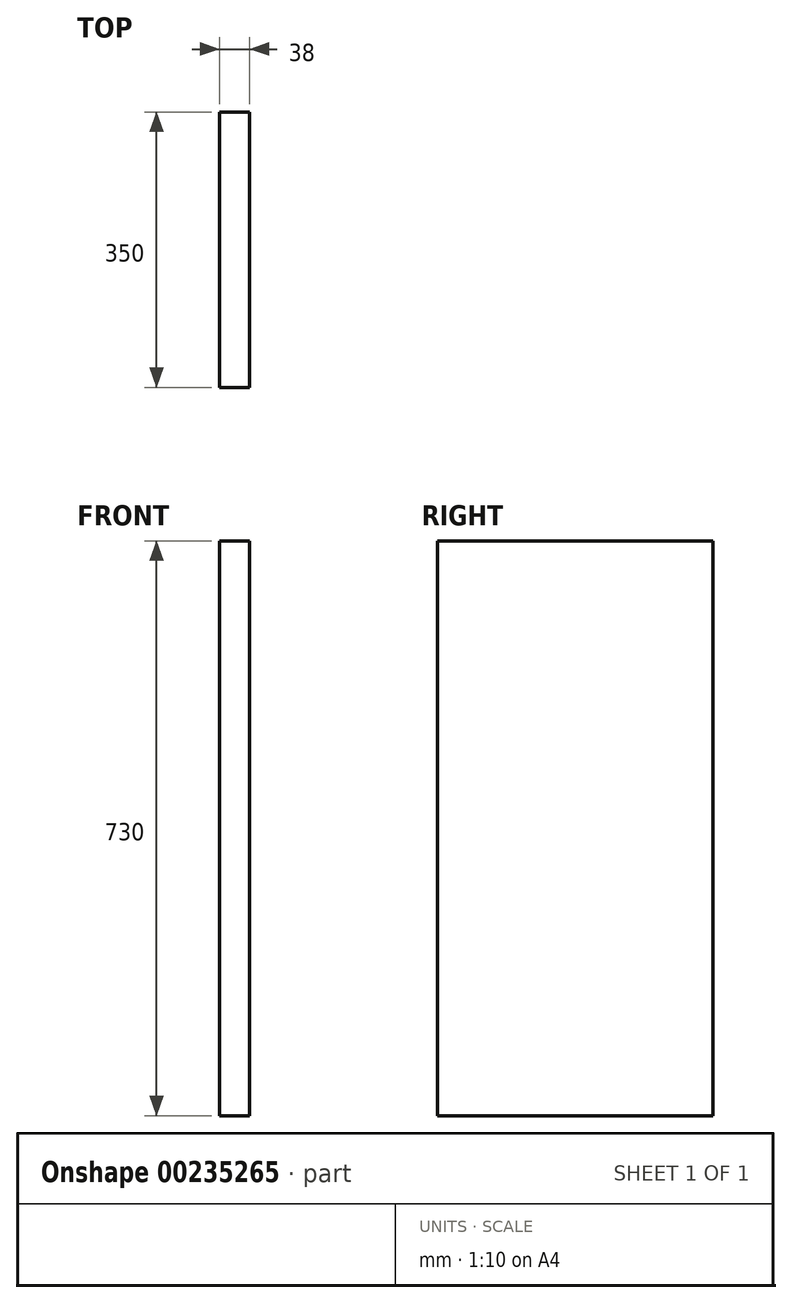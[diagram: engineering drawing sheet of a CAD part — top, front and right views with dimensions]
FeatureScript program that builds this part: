
annotation { "Feature Type Name" : "Feature", "Feature Type Description" : "" }
export const myFeature = defineFeature(function(context is Context, id is Id, definition is map)
    precondition{}
    {
        {
            var Q0;
            Q0=qCreatedBy(makeId("Right.planeOp"),FACE);
            var sketch = newSketch(context, id + "F0", { "sketchPlane" : qUnion([Q0])});
            skLineSegment(sketch, "E0.bottom", {"start": v(0, 0) * mm, "end": v(-350, 0) * mm});
            skLineSegment(sketch, "E0.top", {"start": v(0, 730) * mm, "end": v(-350, 730) * mm});
            skLineSegment(sketch, "E0.left", {"start": v(0, 0) * mm, "end": v(0, 730) * mm});
            skLineSegment(sketch, "E0.right", {"start": v(-350, 0) * mm, "end": v(-350, 730) * mm});
            skSolve(sketch);
        }
        {
            var Q0;
            Q0=makeQuery(id+"F0.imprint","IMPRINT",FACE,{"disambiguationData":[TD([[makeQuery(id+"F0.imprint","IMPRINT",EDGE,{"derivedFrom":sQuery(id+"F0.wireOp",EDGE,"E0.bottom")}),-1.0]])]});
            extrude(context, id + "F1", {"entities" : qUnion([Q0]), "depth" : 38 * mm});
        }
    });
